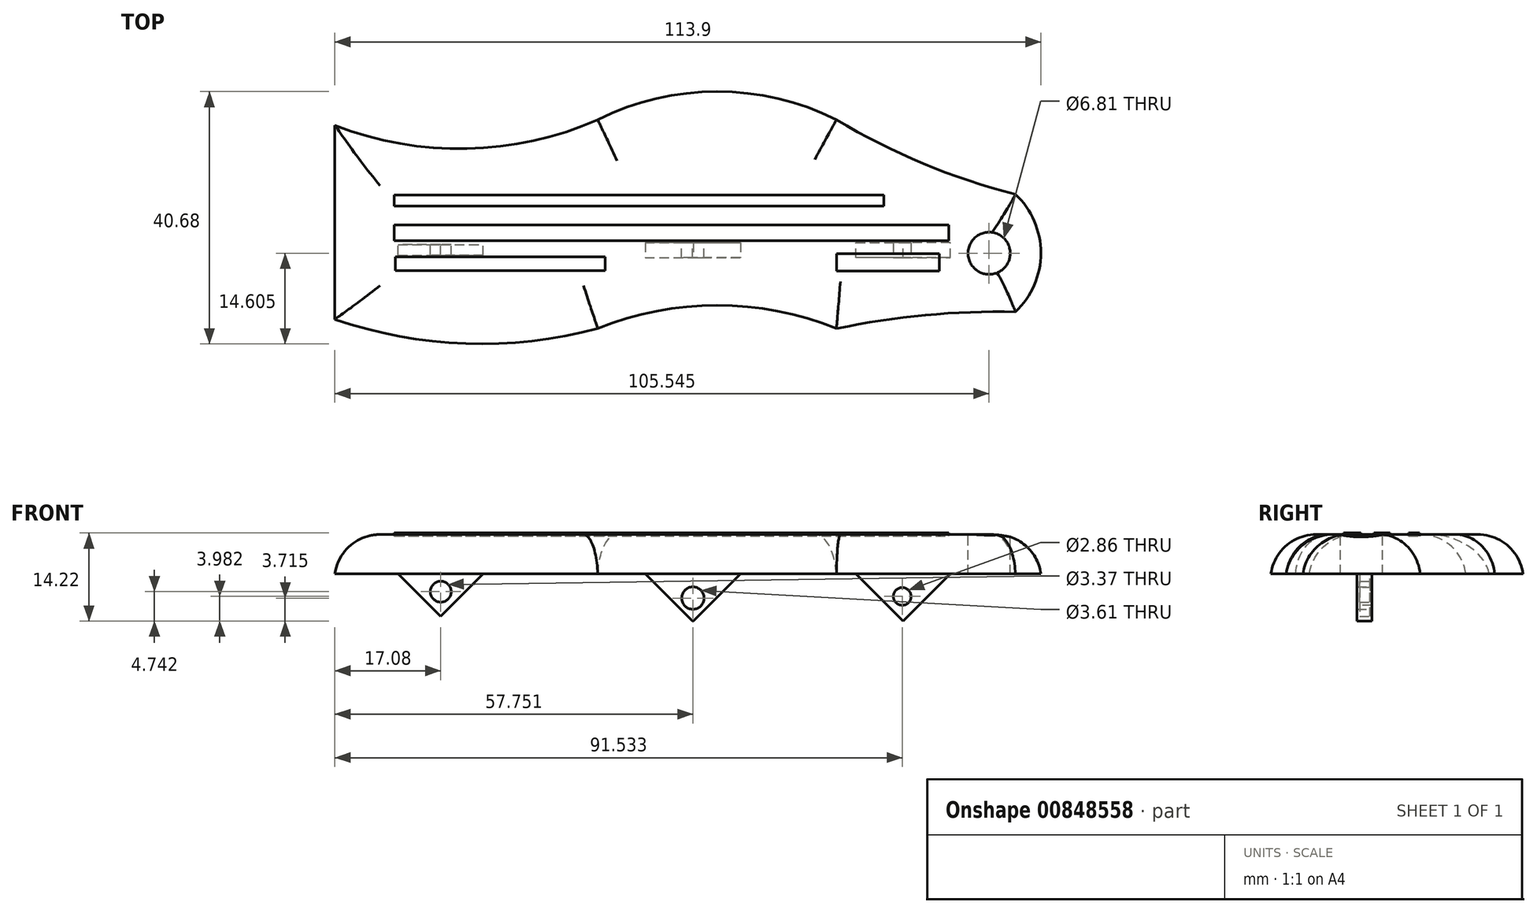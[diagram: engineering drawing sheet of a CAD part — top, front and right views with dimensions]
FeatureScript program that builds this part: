
annotation { "Feature Type Name" : "Feature", "Feature Type Description" : "" }
export const myFeature = defineFeature(function(context is Context, id is Id, definition is map)
    precondition{}
    {
        {
            var Q0;
            Q0=qCreatedBy(makeId("Top.planeOp"),FACE);
            var sketch = newSketch(context, id + "F0", { "sketchPlane" : qUnion([Q0])});
            skArc(sketch, "E0", {"start": v(-64.82, 25.72) * mm, "mid": v(-43.52, 21.94) * mm, "end": v(-22.4, 26.62) * mm});
            skArc(sketch, "E1", {"start": v(16.1, 26.62) * mm, "mid": v(-3.16, 31.16) * mm, "end": v(-22.4, 26.62) * mm});
            skArc(sketch, "E2", {"start": v(-64.82, -5.56) * mm, "mid": v(-43.73, -9.48) * mm, "end": v(-22.4, -7.07) * mm});
            skArc(sketch, "E3", {"start": v(16.1, -7.07) * mm, "mid": v(-3.16, -3.3) * mm, "end": v(-22.4, -7.07) * mm});
            skArc(sketch, "E4", {"start": v(16.1, 26.62) * mm, "mid": v(30.1, 19.55) * mm, "end": v(44.97, 14.59) * mm});
            skArc(sketch, "E5", {"start": v(44.97, -4.36) * mm, "mid": v(30.45, -4.9) * mm, "end": v(16.1, -7.07) * mm});
            skArc(sketch, "E6", {"start": v(44.97, -4.36) * mm, "mid": v(49.08, 5.11) * mm, "end": v(44.97, 14.59) * mm});
            skLineSegment(sketch, "E7", {"start": v(-64.82, 25.72) * mm, "end": v(-64.82, -5.56) * mm});
            skSolve(sketch);
        }
        {
            var Q0;
            Q0 = qSketchRegion(id + "F0", true);
            extrude(context, id + "F1", {"entities" : qUnion([Q0]), "depth" : 6.35 * mm, "offsetDistance" : 25.4 * mm});
        }
        {
            var Q0;
            Q0=makeQuery(id+"F1.opExtrude","CAP_FACE",FACE,{"disambiguationData":[OSD([sQuery(id+"F0.wireOp",EDGE,"E0"),sQuery(id+"F0.wireOp",EDGE,"E1"),sQuery(id+"F0.wireOp",EDGE,"E2"),sQuery(id+"F0.wireOp",EDGE,"E3"),sQuery(id+"F0.wireOp",EDGE,"E4"),sQuery(id+"F0.wireOp",EDGE,"E5"),sQuery(id+"F0.wireOp",EDGE,"E6"),sQuery(id+"F0.wireOp",EDGE,"E7")])],"isStart":false});
            fillet(context, id + "F2", {"entities" : qUnion([Q0]), "radius" : 7.36 * mm, "tangentPropagation" : true, "allowEdgeOverflow" : false});
        }
        {
            var Q0;
            Q0=makeQuery(id+"F1.opExtrude","CAP_FACE",FACE,{"disambiguationData":[OSD([sQuery(id+"F0.wireOp",EDGE,"E0"),sQuery(id+"F0.wireOp",EDGE,"E1"),sQuery(id+"F0.wireOp",EDGE,"E2"),sQuery(id+"F0.wireOp",EDGE,"E3"),sQuery(id+"F0.wireOp",EDGE,"E4"),sQuery(id+"F0.wireOp",EDGE,"E5"),sQuery(id+"F0.wireOp",EDGE,"E6"),sQuery(id+"F0.wireOp",EDGE,"E7")])],"isStart":true});
            var sketch = newSketch(context, id + "F3", { "sketchPlane" : qUnion([Q0])});
            skLineSegment(sketch, "E8.bottom", {"start": v(39.55, -6.77) * mm, "end": v(16.7, -6.77) * mm});
            skLineSegment(sketch, "E8.top", {"start": v(39.55, -4.36) * mm, "end": v(16.7, -4.36) * mm});
            skLineSegment(sketch, "E8.left", {"start": v(39.55, -6.77) * mm, "end": v(39.55, -4.36) * mm});
            skLineSegment(sketch, "E8.right", {"start": v(16.7, -6.77) * mm, "end": v(16.7, -4.36) * mm});
            skSolve(sketch);
        }
        {
            var Q0;
            Q0 = qSketchRegion(id + "F3", true);
            extrude(context, id + "F4", {"entities" : qUnion([Q0]), "operationType" : NewBodyOperationType.ADD, "depth" : 7.62 * mm, "offsetDistance" : 25.4 * mm});
        }
        {
            var Q0;
            Q0=makeQuery(id+"F4.opExtrude","CAP_EDGE",EDGE,{"disambiguationData":[OSD([sQuery(id+"F3.wireOp",EDGE,"E8.right")])],"isStart":false});
            chamfer(context, id + "F5", {"entities" : qUnion([Q0]), "width" : 10.16 * mm, "tangentPropagation" : true});
        }
        {
            var Q0;
            Q0=makeQuery(id+"F4.opExtrude","CAP_EDGE",EDGE,{"disambiguationData":[OSD([sQuery(id+"F3.wireOp",EDGE,"E8.left")])],"isStart":false});
            chamfer(context, id + "F6", {"entities" : qUnion([Q0]), "width" : 12.7 * mm, "tangentPropagation" : true});
        }
        {
            var Q0;
            Q0=makeQuery(id+"F4.opExtrude","SWEPT_FACE",FACE,{"disambiguationData":[OSD([sQuery(id+"F3.wireOp",EDGE,"E8.top")])]});
            var sketch = newSketch(context, id + "F7", { "sketchPlane" : qUnion([Q0])});
            skCircle(sketch, "E9", {"center": v(26.71, -3.64) * mm, "radius": 1.43 * mm});
            skSolve(sketch);
        }
        {
            var Q0;
            Q0 = qSketchRegion(id + "F7", true);
            extrude(context, id + "F8", {"entities" : qUnion([Q0]), "operationType" : NewBodyOperationType.REMOVE, "oppositeDirection" : true, "depth" : 25.4 * mm, "offsetDistance" : 25.4 * mm});
        }
        {
            var Q0;
            Q0=makeQuery(id+"F1.opExtrude","CAP_FACE",FACE,{"disambiguationData":[OSD([sQuery(id+"F0.wireOp",EDGE,"E0"),sQuery(id+"F0.wireOp",EDGE,"E1"),sQuery(id+"F0.wireOp",EDGE,"E2"),sQuery(id+"F0.wireOp",EDGE,"E3"),sQuery(id+"F0.wireOp",EDGE,"E4"),sQuery(id+"F0.wireOp",EDGE,"E5"),sQuery(id+"F0.wireOp",EDGE,"E6"),sQuery(id+"F0.wireOp",EDGE,"E7")])],"isStart":true});
            var sketch = newSketch(context, id + "F9", { "sketchPlane" : qUnion([Q0])});
            skLineSegment(sketch, "E10.bottom", {"start": v(-54.62, -4.78) * mm, "end": v(-40.9, -4.78) * mm});
            skLineSegment(sketch, "E10.top", {"start": v(-54.62, -6.49) * mm, "end": v(-40.9, -6.49) * mm});
            skLineSegment(sketch, "E10.left", {"start": v(-54.62, -4.78) * mm, "end": v(-54.62, -6.49) * mm});
            skLineSegment(sketch, "E10.right", {"start": v(-40.9, -4.78) * mm, "end": v(-40.9, -6.49) * mm});
            skSolve(sketch);
        }
        {
            var Q0;
            Q0 = qSketchRegion(id + "F9", true);
            extrude(context, id + "F10", {"entities" : qUnion([Q0]), "operationType" : NewBodyOperationType.ADD, "depth" : 7.62 * mm, "offsetDistance" : 25.4 * mm});
        }
        {
            var Q0;
            Q0=makeQuery(id+"F10.opExtrude","CAP_EDGE",EDGE,{"disambiguationData":[OSD([sQuery(id+"F9.wireOp",EDGE,"E10.left")])],"isStart":false});
            var Q1;
            Q1=makeQuery(id+"F10.opExtrude","CAP_EDGE",EDGE,{"disambiguationData":[OSD([sQuery(id+"F9.wireOp",EDGE,"E10.right")])],"isStart":false});
            chamfer(context, id + "F11", {"entities" : qUnion([Q0, Q1]), "width" : 7.62 * mm, "tangentPropagation" : true});
        }
        {
            var Q0;
            Q0=makeQuery(id+"F10.opExtrude","SWEPT_FACE",FACE,{"disambiguationData":[OSD([sQuery(id+"F9.wireOp",EDGE,"E10.top")])]});
            var sketch = newSketch(context, id + "F12", { "sketchPlane" : qUnion([Q0])});
            skCircle(sketch, "E11", {"center": v(47.74, -2.88) * mm, "radius": 1.68 * mm});
            skSolve(sketch);
        }
        {
            var Q0;
            Q0 = qSketchRegion(id + "F12", true);
            extrude(context, id + "F13", {"entities" : qUnion([Q0]), "operationType" : NewBodyOperationType.REMOVE, "oppositeDirection" : true, "depth" : 25.4 * mm, "offsetDistance" : 25.4 * mm});
        }
        {
            var Q0;
            Q0=qCreatedBy(makeId("Top.planeOp"),FACE);
            cPlane(context, id + "F14", {"entities" : qUnion([Q0]), "cplaneType" : CPlaneType.OFFSET, "offset" : 6.6 * mm, "width" : 152.4 * mm, "height" : 152.4 * mm});
        }
        {
            var Q0;
            Q0=qCreatedBy(id+"F14.planeOp",FACE);
            var sketch = newSketch(context, id + "F15", { "sketchPlane" : qUnion([Q0])});
            skCircle(sketch, "E12", {"center": v(40.73, 5.08) * mm, "radius": 3.4 * mm});
            skSolve(sketch);
        }
        {
            var Q0;
            Q0 = qSketchRegion(id + "F15", true);
            extrude(context, id + "F16", {"entities" : qUnion([Q0]), "operationType" : NewBodyOperationType.REMOVE, "oppositeDirection" : true, "depth" : 25.4 * mm, "offsetDistance" : 25.4 * mm});
        }
        {
            var Q0;
            Q0=qCreatedBy(id+"F14.planeOp",FACE);
            var sketch = newSketch(context, id + "F17", { "sketchPlane" : qUnion([Q0])});
            skLineSegment(sketch, "E13.bottom", {"start": v(-55.28, 9.68) * mm, "end": v(34.23, 9.68) * mm});
            skLineSegment(sketch, "E13.top", {"start": v(-55.28, 7.1) * mm, "end": v(34.23, 7.1) * mm});
            skLineSegment(sketch, "E13.left", {"start": v(-55.28, 9.68) * mm, "end": v(-55.28, 7.1) * mm});
            skLineSegment(sketch, "E13.right", {"start": v(34.23, 9.68) * mm, "end": v(34.23, 7.1) * mm});
            skLineSegment(sketch, "E14.bottom", {"start": v(-55.28, 12.68) * mm, "end": v(23.73, 12.68) * mm});
            skLineSegment(sketch, "E14.top", {"start": v(-55.28, 14.48) * mm, "end": v(23.73, 14.48) * mm});
            skLineSegment(sketch, "E14.left", {"start": v(-55.28, 12.68) * mm, "end": v(-55.28, 14.48) * mm});
            skLineSegment(sketch, "E14.right", {"start": v(23.73, 12.68) * mm, "end": v(23.73, 14.48) * mm});
            skLineSegment(sketch, "E15.bottom", {"start": v(-55.06, 2.26) * mm, "end": v(-21.23, 2.26) * mm});
            skLineSegment(sketch, "E15.top", {"start": v(-55.06, 4.51) * mm, "end": v(-21.23, 4.51) * mm});
            skLineSegment(sketch, "E15.left", {"start": v(-55.06, 2.26) * mm, "end": v(-55.06, 4.51) * mm});
            skLineSegment(sketch, "E15.right", {"start": v(-21.23, 2.26) * mm, "end": v(-21.23, 4.51) * mm});
            skLineSegment(sketch, "E16.bottom", {"start": v(16.15, 2.21) * mm, "end": v(32.7, 2.21) * mm});
            skLineSegment(sketch, "E16.top", {"start": v(16.15, 5.03) * mm, "end": v(32.7, 5.03) * mm});
            skLineSegment(sketch, "E16.left", {"start": v(16.15, 2.21) * mm, "end": v(16.15, 5.03) * mm});
            skLineSegment(sketch, "E16.right", {"start": v(32.7, 2.21) * mm, "end": v(32.7, 5.03) * mm});
            skSolve(sketch);
        }
        {
            var Q0;
            Q0 = qSketchRegion(id + "F17", true);
            extrude(context, id + "F18", {"entities" : qUnion([Q0]), "oppositeDirection" : true, "depth" : 0.5 * mm, "offsetDistance" : 25.4 * mm});
        }
        {
            var Q0;
            Q0=makeQuery(id+"F1.opExtrude","CAP_FACE",FACE,{"disambiguationData":[OSD([sQuery(id+"F0.wireOp",EDGE,"E0"),sQuery(id+"F0.wireOp",EDGE,"E1"),sQuery(id+"F0.wireOp",EDGE,"E2"),sQuery(id+"F0.wireOp",EDGE,"E3"),sQuery(id+"F0.wireOp",EDGE,"E4"),sQuery(id+"F0.wireOp",EDGE,"E5"),sQuery(id+"F0.wireOp",EDGE,"E6"),sQuery(id+"F0.wireOp",EDGE,"E7")])],"isStart":true});
            var sketch = newSketch(context, id + "F19", { "sketchPlane" : qUnion([Q0])});
            skLineSegment(sketch, "E17.bottom", {"start": v(-17.3, -4.36) * mm, "end": v(3.16, -4.36) * mm});
            skLineSegment(sketch, "E17.top", {"start": v(-17.3, -6.77) * mm, "end": v(3.16, -6.77) * mm});
            skLineSegment(sketch, "E17.left", {"start": v(-17.3, -4.36) * mm, "end": v(-17.3, -6.77) * mm});
            skLineSegment(sketch, "E17.right", {"start": v(3.16, -4.36) * mm, "end": v(3.16, -6.77) * mm});
            skSolve(sketch);
        }
        {
            var Q0;
            Q0 = qSketchRegion(id + "F19", true);
            extrude(context, id + "F20", {"entities" : qUnion([Q0]), "operationType" : NewBodyOperationType.ADD, "depth" : 7.62 * mm, "offsetDistance" : 25.4 * mm});
        }
        {
            var Q0;
            Q0=makeQuery(id+"F20.opExtrude","CAP_EDGE",EDGE,{"disambiguationData":[OSD([sQuery(id+"F19.wireOp",EDGE,"E17.left")])],"isStart":false});
            var Q1;
            Q1=makeQuery(id+"F20.opExtrude","CAP_EDGE",EDGE,{"disambiguationData":[OSD([sQuery(id+"F19.wireOp",EDGE,"E17.right")])],"isStart":false});
            chamfer(context, id + "F21", {"entities" : qUnion([Q0, Q1]), "width" : 10.16 * mm, "tangentPropagation" : true});
        }
        {
            var Q0;
            Q0=makeQuery(id+"F20.opExtrude","SWEPT_FACE",FACE,{"disambiguationData":[OSD([sQuery(id+"F19.wireOp",EDGE,"E17.top")])]});
            var sketch = newSketch(context, id + "F22", { "sketchPlane" : qUnion([Q0])});
            skCircle(sketch, "E18", {"center": v(7.07, -3.9) * mm, "radius": 1.8 * mm});
            skPoint(sketch, "E18.centerSnap0", {"position": v(7.07, 0) * mm});
            skSolve(sketch);
        }
        {
            var Q0;
            Q0 = qSketchRegion(id + "F22", true);
            extrude(context, id + "F23", {"entities" : qUnion([Q0]), "operationType" : NewBodyOperationType.REMOVE, "oppositeDirection" : true, "depth" : 25.4 * mm, "offsetDistance" : 25.4 * mm});
        }
    });
